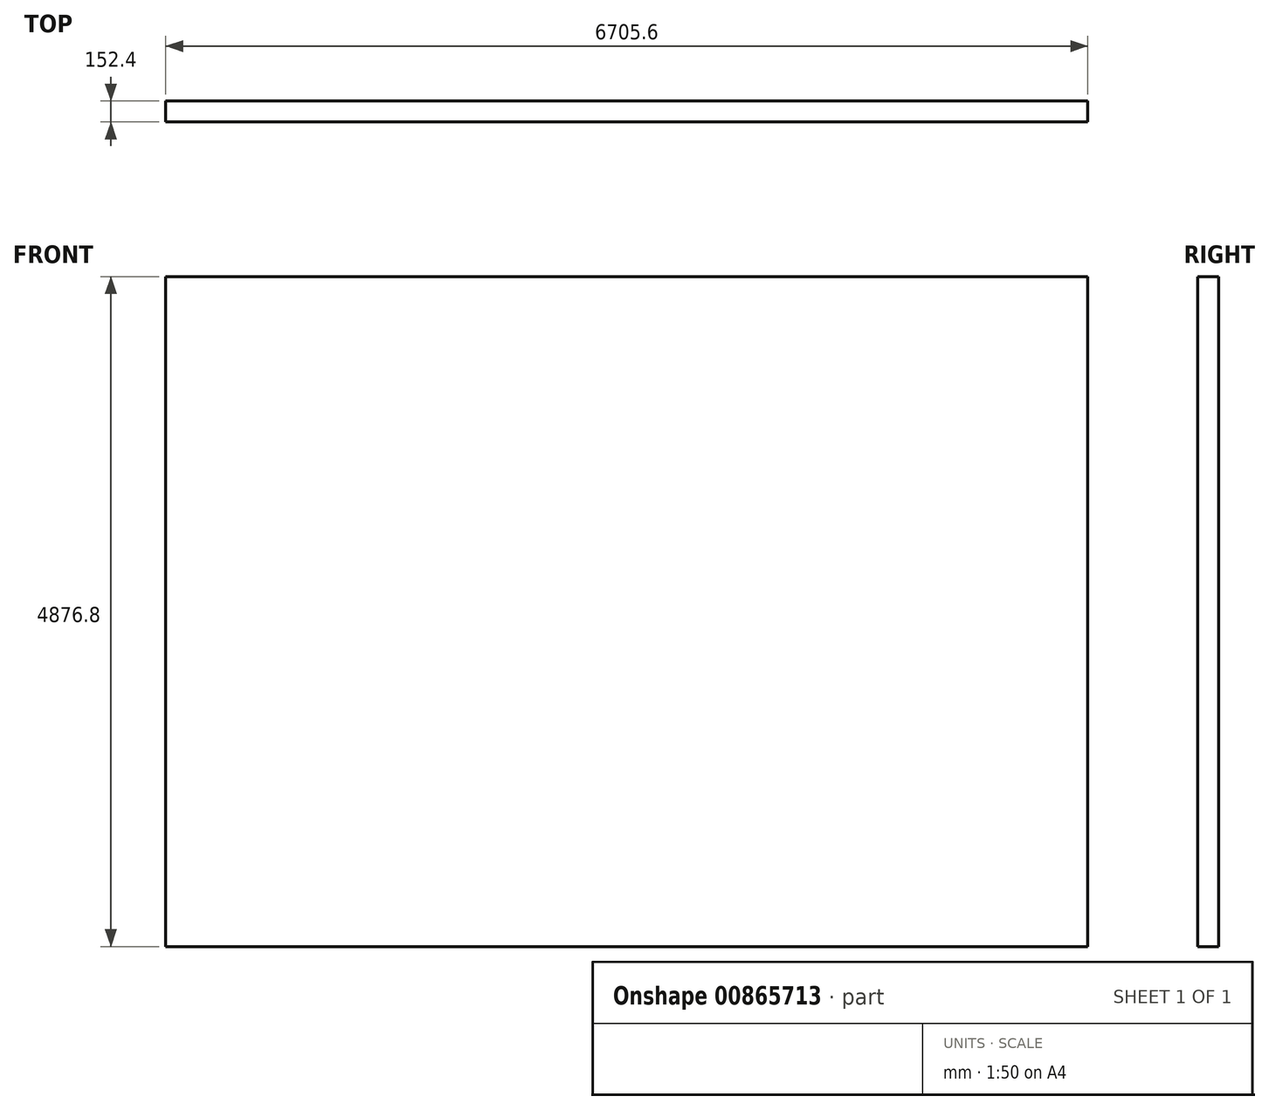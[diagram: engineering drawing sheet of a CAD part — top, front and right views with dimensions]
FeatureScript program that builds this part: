
annotation { "Feature Type Name" : "Feature", "Feature Type Description" : "" }
export const myFeature = defineFeature(function(context is Context, id is Id, definition is map)
    precondition{}
    {
        {
            var Q0;
            Q0=qCreatedBy(makeId("Front.planeOp"),FACE);
            var sketch = newSketch(context, id + "F0", { "sketchPlane" : qUnion([Q0])});
            skLineSegment(sketch, "E0.bottom", {"start": v(0, 0) * mm, "end": v(6705.6, 0) * mm});
            skLineSegment(sketch, "E0.top", {"start": v(0, 4876.8) * mm, "end": v(6705.6, 4876.8) * mm});
            skLineSegment(sketch, "E0.left", {"start": v(0, 0) * mm, "end": v(0, 4876.8) * mm});
            skLineSegment(sketch, "E0.right", {"start": v(6705.6, 0) * mm, "end": v(6705.6, 4876.8) * mm});
            skSolve(sketch);
        }
        {
            var Q0;
            Q0=makeQuery(id+"F0.imprint","IMPRINT",FACE,{"disambiguationData":[TD([[makeQuery(id+"F0.imprint","IMPRINT",EDGE,{"derivedFrom":sQuery(id+"F0.wireOp",EDGE,"E0.bottom")}),1.0]])]});
            extrude(context, id + "F1", {"entities" : qUnion([Q0]), "depth" : 152.4 * mm, "offsetDistance" : 25.4 * mm});
        }
    });
